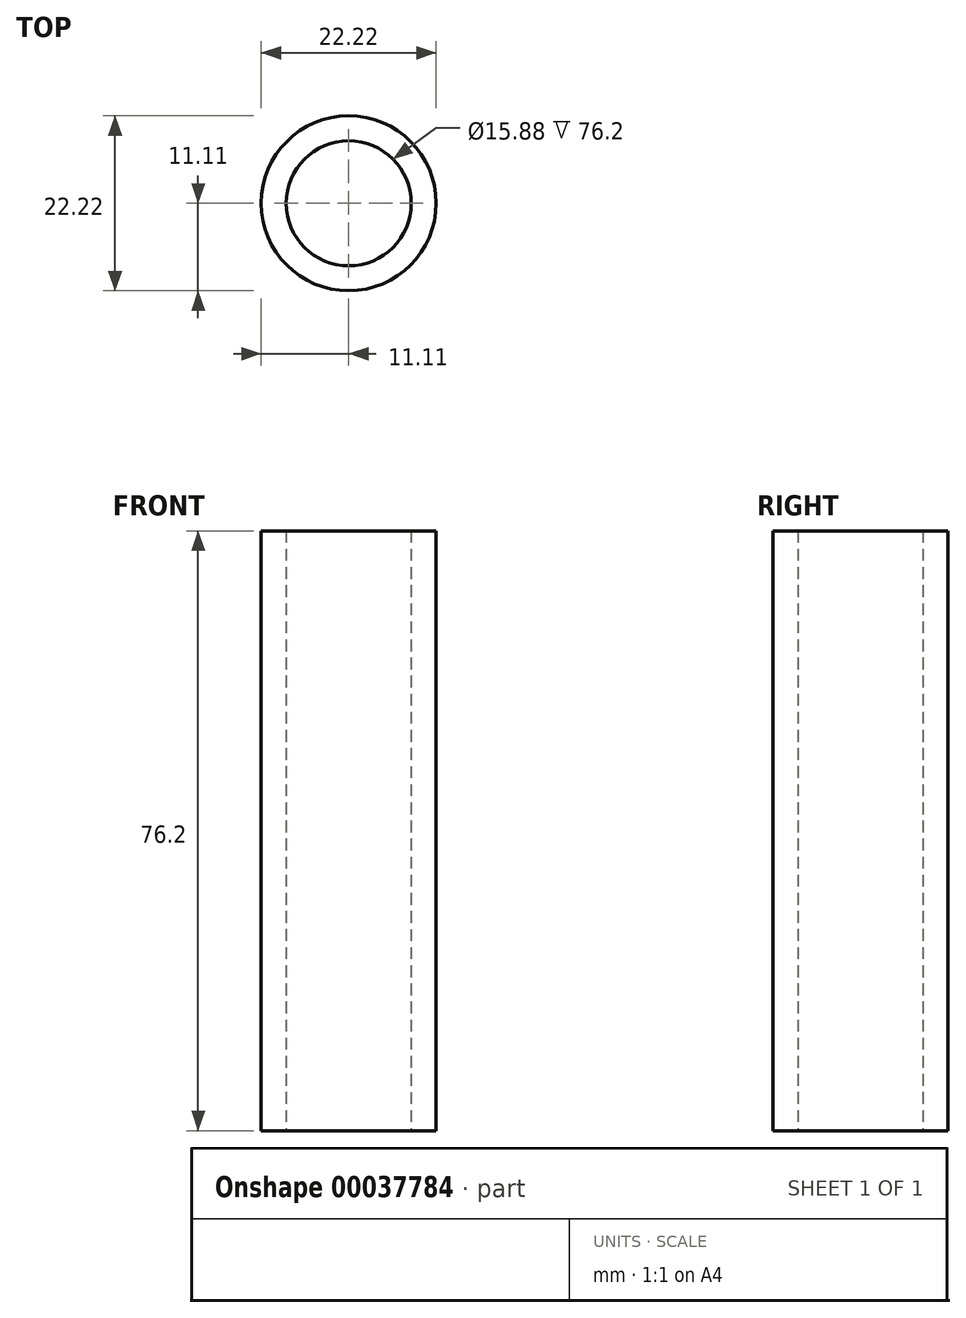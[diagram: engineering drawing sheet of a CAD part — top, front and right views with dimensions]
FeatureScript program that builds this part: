
annotation { "Feature Type Name" : "Feature", "Feature Type Description" : "" }
export const myFeature = defineFeature(function(context is Context, id is Id, definition is map)
    precondition{}
    {
        {
            var Q0;
            Q0=qCreatedBy(makeId("Top.planeOp"),FACE);
            var sketch = newSketch(context, id + "F0", { "sketchPlane" : qUnion([Q0])});
            skCircle(sketch, "E0", {"center": v(0, 0) * mm, "radius": 7.94 * mm});
            skCircle(sketch, "E1", {"center": v(0, 0) * mm, "radius": 11.11 * mm});
            skSolve(sketch);
        }
        {
            var Q0;
            Q0 = qSketchRegion(id + "F0", true);
            extrude(context, id + "F1", {"entities" : qUnion([Q0]), "depth" : 76.2 * mm});
        }
    });
